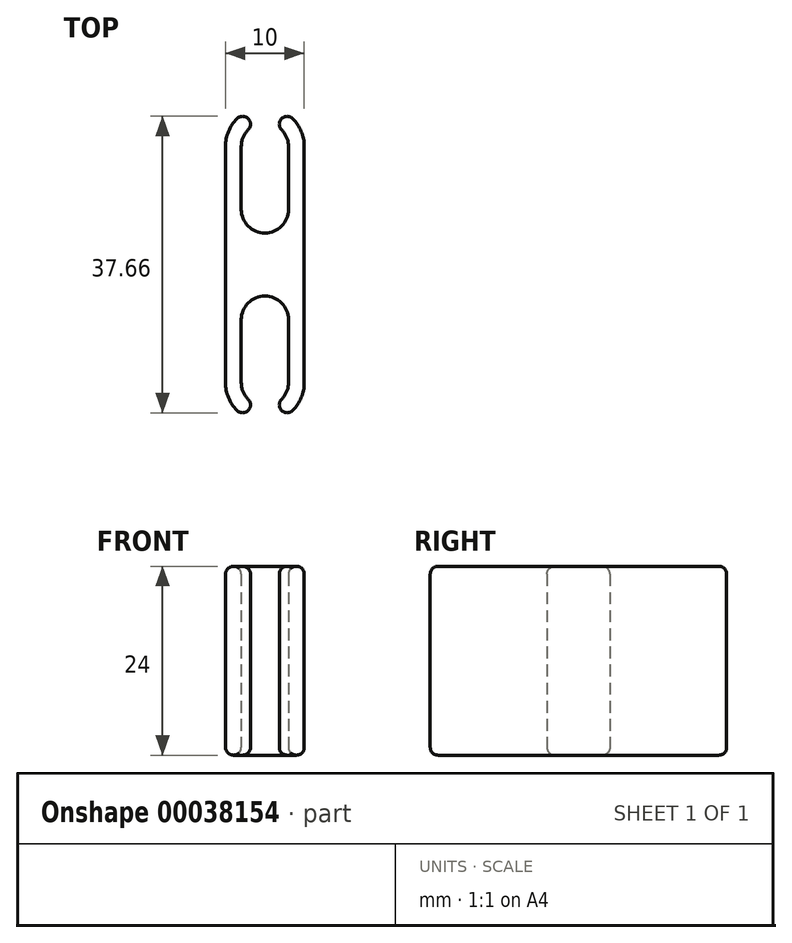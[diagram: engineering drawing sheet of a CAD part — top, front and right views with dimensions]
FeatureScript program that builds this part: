
annotation { "Feature Type Name" : "Feature", "Feature Type Description" : "" }
export const myFeature = defineFeature(function(context is Context, id is Id, definition is map)
    precondition{}
    {
        {
            var Q0;
            Q0=qCreatedBy(makeId("Top.planeOp"),FACE);
            var sketch = newSketch(context, id + "F0", { "sketchPlane" : qUnion([Q0])});
            skLineSegment(sketch, "E0.rect.bottom", {"start": v(5, 15) * mm, "end": v(-5, 15) * mm, "construction": true});
            skLineSegment(sketch, "E0.rect.top", {"start": v(5, -15) * mm, "end": v(-5, -15) * mm, "construction": true});
            skLineSegment(sketch, "E0.rect.left", {"start": v(5, 15) * mm, "end": v(5, -15) * mm, "construction": true});
            skLineSegment(sketch, "E0.rect.right", {"start": v(-5, 15) * mm, "end": v(-5, -15) * mm, "construction": true});
            skPoint(sketch, "E0.rect.middle", {"position": v(0, 0) * mm});
            skLineSegment(sketch, "E1", {"start": v(0, 41.3) * mm, "end": v(0, -38.86) * mm, "construction": true});
            skLineSegment(sketch, "E2", {"start": v(-25.67, 0) * mm, "end": v(24.78, 0) * mm, "construction": true});
            skArc(sketch, "E3", {"start": v(-3.54, 18.54) * mm, "mid": v(-4.62, 16.91) * mm, "end": v(-5, 15) * mm});
            skArc(sketch, "E4", {"start": v(-2.12, 17.12) * mm, "mid": v(-2.77, 16.15) * mm, "end": v(-3, 15) * mm});
            skLineSegment(sketch, "E5.rect.bottom", {"start": v(5, 20) * mm, "end": v(-5, 20) * mm, "construction": true});
            skLineSegment(sketch, "E5.rect.top", {"start": v(5, -20) * mm, "end": v(-5, -20) * mm, "construction": true});
            skLineSegment(sketch, "E5.rect.left", {"start": v(5, 20) * mm, "end": v(5, -20) * mm, "construction": true});
            skLineSegment(sketch, "E5.rect.right", {"start": v(-5, 20) * mm, "end": v(-5, -20) * mm, "construction": true});
            skLineSegment(sketch, "E6", {"start": v(0, 15) * mm, "end": v(-5, 20) * mm, "construction": true});
            skLineSegment(sketch, "E7", {"start": v(-2.12, 17.12) * mm, "end": v(-3.54, 18.54) * mm, "construction": true});
            skArc(sketch, "E8", {"start": v(-2.12, 17.12) * mm, "mid": v(-2.12, 18.54) * mm, "end": v(-3.54, 18.54) * mm});
            skLineSegment(sketch, "E9", {"start": v(-5, 15) * mm, "end": v(-5, 0) * mm});
            skLineSegment(sketch, "E10", {"start": v(-3, 15) * mm, "end": v(-3, 0) * mm, "construction": true});
            skLineSegment(sketch, "E11.bottom", {"start": v(-5, 0) * mm, "end": v(5, 0) * mm, "construction": true});
            skLineSegment(sketch, "E11.top", {"start": v(-5, 7) * mm, "end": v(5, 7) * mm, "construction": true});
            skLineSegment(sketch, "E11.left", {"start": v(-5, 0) * mm, "end": v(-5, 7) * mm, "construction": true});
            skLineSegment(sketch, "E11.right", {"start": v(5, 0) * mm, "end": v(5, 7) * mm, "construction": true});
            skArc(sketch, "E12", {"start": v(-3, 7) * mm, "mid": v(-2.12, 4.88) * mm, "end": v(0, 4) * mm});
            skLineSegment(sketch, "E13", {"start": v(-3, 15) * mm, "end": v(-3, 7) * mm});
            skArc(sketch, "E14.MirrorCS", {"start": v(3.54, 18.54) * mm, "mid": v(4.62, 16.91) * mm, "end": v(5, 15) * mm});
            skArc(sketch, "E15.MirrorCS", {"start": v(2.12, 17.12) * mm, "mid": v(2.12, 18.54) * mm, "end": v(3.54, 18.54) * mm});
            skArc(sketch, "E16.MirrorCS", {"start": v(2.12, 17.12) * mm, "mid": v(2.77, 16.15) * mm, "end": v(3, 15) * mm});
            skLineSegment(sketch, "E17.MirrorCS", {"start": v(3, 15) * mm, "end": v(3, 7) * mm});
            skLineSegment(sketch, "E18.MirrorCS", {"start": v(5, 15) * mm, "end": v(5, 0) * mm});
            skArc(sketch, "E19.MirrorCS", {"start": v(3, 7) * mm, "mid": v(2.12, 4.88) * mm, "end": v(0, 4) * mm});
            skLineSegment(sketch, "E20.MirrorCS", {"start": v(-5, -15) * mm, "end": v(-5, 0) * mm});
            skArc(sketch, "E21.MirrorCS", {"start": v(-3.54, -18.54) * mm, "mid": v(-4.62, -16.91) * mm, "end": v(-5, -15) * mm});
            skArc(sketch, "E22.MirrorCS", {"start": v(-2.12, -17.12) * mm, "mid": v(-2.12, -18.54) * mm, "end": v(-3.54, -18.54) * mm});
            skArc(sketch, "E23.MirrorCS", {"start": v(-2.12, -17.12) * mm, "mid": v(-2.77, -16.15) * mm, "end": v(-3, -15) * mm});
            skLineSegment(sketch, "E24.MirrorCS", {"start": v(-3, -15) * mm, "end": v(-3, -7) * mm});
            skArc(sketch, "E25.MirrorCS", {"start": v(-3, -7) * mm, "mid": v(-2.12, -4.88) * mm, "end": v(0, -4) * mm});
            skArc(sketch, "E26.MirrorCS", {"start": v(3, -7) * mm, "mid": v(2.12, -4.88) * mm, "end": v(0, -4) * mm});
            skLineSegment(sketch, "E27.MirrorCS", {"start": v(3, -15) * mm, "end": v(3, -7) * mm});
            skArc(sketch, "E28.MirrorCS", {"start": v(2.12, -17.12) * mm, "mid": v(2.77, -16.15) * mm, "end": v(3, -15) * mm});
            skArc(sketch, "E29.MirrorCS", {"start": v(2.12, -17.12) * mm, "mid": v(2.12, -18.54) * mm, "end": v(3.54, -18.54) * mm});
            skArc(sketch, "E30.MirrorCS", {"start": v(3.54, -18.54) * mm, "mid": v(4.62, -16.91) * mm, "end": v(5, -15) * mm});
            skLineSegment(sketch, "E31.MirrorCS", {"start": v(5, -15) * mm, "end": v(5, 0) * mm});
            skSolve(sketch);
        }
        {
            assignVariable(context, id + "F1", {"name" : "altura", "anyValue" : 24});
        }
        {
            var Q0;
            Q0 = qSketchRegion(id + "F0", true);
            extrude(context, id + "F2", {"entities" : qUnion([Q0]), "depth" : (getVariable(context, 'altura')) * mm});
        }
        {
            var Q0;
            Q0=makeQuery(id+"F2.opExtrude","CAP_FACE",FACE,{"disambiguationData":[OSD([sQuery(id+"F0.wireOp",EDGE,"E4"),sQuery(id+"F0.wireOp",EDGE,"E8"),sQuery(id+"F0.wireOp",EDGE,"E3"),sQuery(id+"F0.wireOp",EDGE,"E9"),sQuery(id+"F0.wireOp",EDGE,"E12"),sQuery(id+"F0.wireOp",EDGE,"E13"),sQuery(id+"F0.wireOp",EDGE,"E14.MirrorCS"),sQuery(id+"F0.wireOp",EDGE,"E15.MirrorCS"),sQuery(id+"F0.wireOp",EDGE,"E16.MirrorCS"),sQuery(id+"F0.wireOp",EDGE,"E17.MirrorCS"),sQuery(id+"F0.wireOp",EDGE,"E18.MirrorCS"),sQuery(id+"F0.wireOp",EDGE,"E19.MirrorCS"),sQuery(id+"F0.wireOp",EDGE,"E21.MirrorCS"),sQuery(id+"F0.wireOp",EDGE,"E22.MirrorCS"),sQuery(id+"F0.wireOp",EDGE,"E20.MirrorCS"),sQuery(id+"F0.wireOp",EDGE,"E23.MirrorCS"),sQuery(id+"F0.wireOp",EDGE,"E24.MirrorCS"),sQuery(id+"F0.wireOp",EDGE,"E25.MirrorCS"),sQuery(id+"F0.wireOp",EDGE,"E26.MirrorCS"),sQuery(id+"F0.wireOp",EDGE,"E27.MirrorCS"),sQuery(id+"F0.wireOp",EDGE,"E28.MirrorCS"),sQuery(id+"F0.wireOp",EDGE,"E29.MirrorCS"),sQuery(id+"F0.wireOp",EDGE,"E30.MirrorCS"),sQuery(id+"F0.wireOp",EDGE,"E31.MirrorCS")])],"isStart":false});
            var Q1;
            Q1=makeQuery(id+"F2.opExtrude","CAP_FACE",FACE,{"disambiguationData":[OSD([sQuery(id+"F0.wireOp",EDGE,"E4"),sQuery(id+"F0.wireOp",EDGE,"E8"),sQuery(id+"F0.wireOp",EDGE,"E3"),sQuery(id+"F0.wireOp",EDGE,"E9"),sQuery(id+"F0.wireOp",EDGE,"E12"),sQuery(id+"F0.wireOp",EDGE,"E13"),sQuery(id+"F0.wireOp",EDGE,"E14.MirrorCS"),sQuery(id+"F0.wireOp",EDGE,"E15.MirrorCS"),sQuery(id+"F0.wireOp",EDGE,"E16.MirrorCS"),sQuery(id+"F0.wireOp",EDGE,"E17.MirrorCS"),sQuery(id+"F0.wireOp",EDGE,"E18.MirrorCS"),sQuery(id+"F0.wireOp",EDGE,"E19.MirrorCS"),sQuery(id+"F0.wireOp",EDGE,"E21.MirrorCS"),sQuery(id+"F0.wireOp",EDGE,"E22.MirrorCS"),sQuery(id+"F0.wireOp",EDGE,"E20.MirrorCS"),sQuery(id+"F0.wireOp",EDGE,"E23.MirrorCS"),sQuery(id+"F0.wireOp",EDGE,"E24.MirrorCS"),sQuery(id+"F0.wireOp",EDGE,"E25.MirrorCS"),sQuery(id+"F0.wireOp",EDGE,"E26.MirrorCS"),sQuery(id+"F0.wireOp",EDGE,"E27.MirrorCS"),sQuery(id+"F0.wireOp",EDGE,"E28.MirrorCS"),sQuery(id+"F0.wireOp",EDGE,"E29.MirrorCS"),sQuery(id+"F0.wireOp",EDGE,"E30.MirrorCS"),sQuery(id+"F0.wireOp",EDGE,"E31.MirrorCS")])],"isStart":true});
            fillet(context, id + "F3", {"entities" : qUnion([Q0, Q1]), "radius" : 1 * mm, "tangentPropagation" : true, "allowEdgeOverflow" : false});
        }
    });
